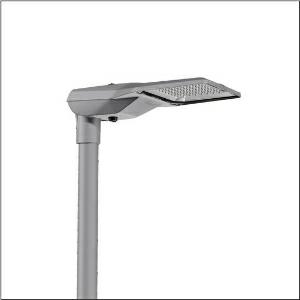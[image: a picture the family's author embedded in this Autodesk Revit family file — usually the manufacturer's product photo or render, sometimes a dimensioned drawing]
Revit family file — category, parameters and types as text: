
# Revit family: streetlight_sl_21_iq_midi___st1_0a_5xe3d41y08nb_87cf
name_source: partatom
category: Lighting Fixtures
units: mm (PartAtom-declared; Revit-internal decimal feet)

## family parameters
Cut with Voids When Loaded = No
Host = Face
Light Source = No
Part Type = Normal
Room Calculation Point = No
Round Connector Dimension = Use Diameter
Shared = No

## types (1)
- --- (1 x LED, 22330 lm, 136.6 W, 4000K)
    Apparent Load = 137 VA
    CIE Flux Codes = 40 73 97 100 100
    Color Rendering = 70
    Color Temperature = 4000K
    Default Elevation = 1800 mm
    Description = Streetlight SL 21 iQ midi, mast luminaire, primary light control with lens, of PMMA, primary optical cover: cover, of toughened safety glass, transparent, light distribution: ST1.0a, light emission: direct distribution, primary light characteristic: asymmetric, installation type: post-top, side-entry, LED, High Power LED, rated luminous flux: 22.330lm, luminous efficacy: 164lm/W, light colour: 740, colour temperature: 4000K, control gear: iQ-Street Remote, D4i with power reduction, control: pre-setting: logarithmic dimming characteristic, Street-Remote, Auto-Match, Temp-Guard, Lumen-Switch, Night-Set, Smart-Wire, Light-Fading, Desk-Remote (wireless, voltage-free reading and setting of iQ features in the workshop via application-optimized NFC function/RFID function), optimised constant luminous flux control (CLO 2.0), mains connection: 230..240V, AC, 50/60Hz, start of lifetime: 137W, end of service life: 144W, reduction: 62W, luminaire housing, of diecast aluminium, powder-coated, Siteco® metallic grey (DB 702S), corrosivity category C5 mid according to DIN EN ISO 12944, please order mast flange separately, inclination adjustable: 0°, 5°, 10°, 15°, sealing non-destructively replaceable, multi-level sealing system, length: 644mm, width: 335mm, height: 110mm, mast flange for spigot size: 42mm (side-entry): 5XC10008XM4, 60/48mm (side-entry/post-top): 5XC10108XM2, 76/60mm (side-entry/post-top): 5XC10108XM1, mounting height: 4..8m, Smart Interface below and above, protection rating (complete): IP66, insulation class (complete): insulation class II (safety insulation), certification: CE, ENEC, ENEC+, VDE, impact resistance: IK10, permissible operating ambient temperature for outdoor applications: -40..+50°C, standard-compliant lighting for roads and squares, packaging unit: 1 piece

Light Distribution: ST1.0a
    Height = 111 mm
    Lamp = 1 x LED
    Lamp Light Flux = 22330 lm
    Lamp Power = 136.6 W
    Lamp count = 1
    Length = 644 mm
    Luminous efficacy = 163 lm/W
    Manufacturer = Siteco
    ModVariant = No
    Model = 5XE3D41Y08NB
    Number of Poles = 1
    OnlyDefault = Yes
    Power Factor = 1
    Product Name = Streetlight SL 21 iQ midi | ST1.0a
    Product group = mast luminaire | pylon top
    ProductGroupID = 6100
    Protection Class = Protection class II
    Protection Degree = IP 66
    RLX_Detail_Level = 1
    RLX_Emergency_Light_Flux = 0 lm
    RLX_Emergency_Type = 0
    RLX_Emergency_Type_DB = No
    RlxData = <blob elided: 90945 chars, md5=5665304b>
    Socket = socket
    Standby Power = 0 W
    System Light Flux = 22330 lm
    System Power = 137 W
    Type Comments = factory setting: luminous flux: 100 % | dim-lin: 254 | 733 mA
    Type Image = l_1004304.jpg
    URL = http://relux.com
    VarID = @adj_135207
    Voltage = 0 V
    Weight = 0.00 kg
    Width = 336 mm

## geometry (parser evidence)
native form markers: Blend x4, Sweep x10
no freeform markers — native parametric forms only
